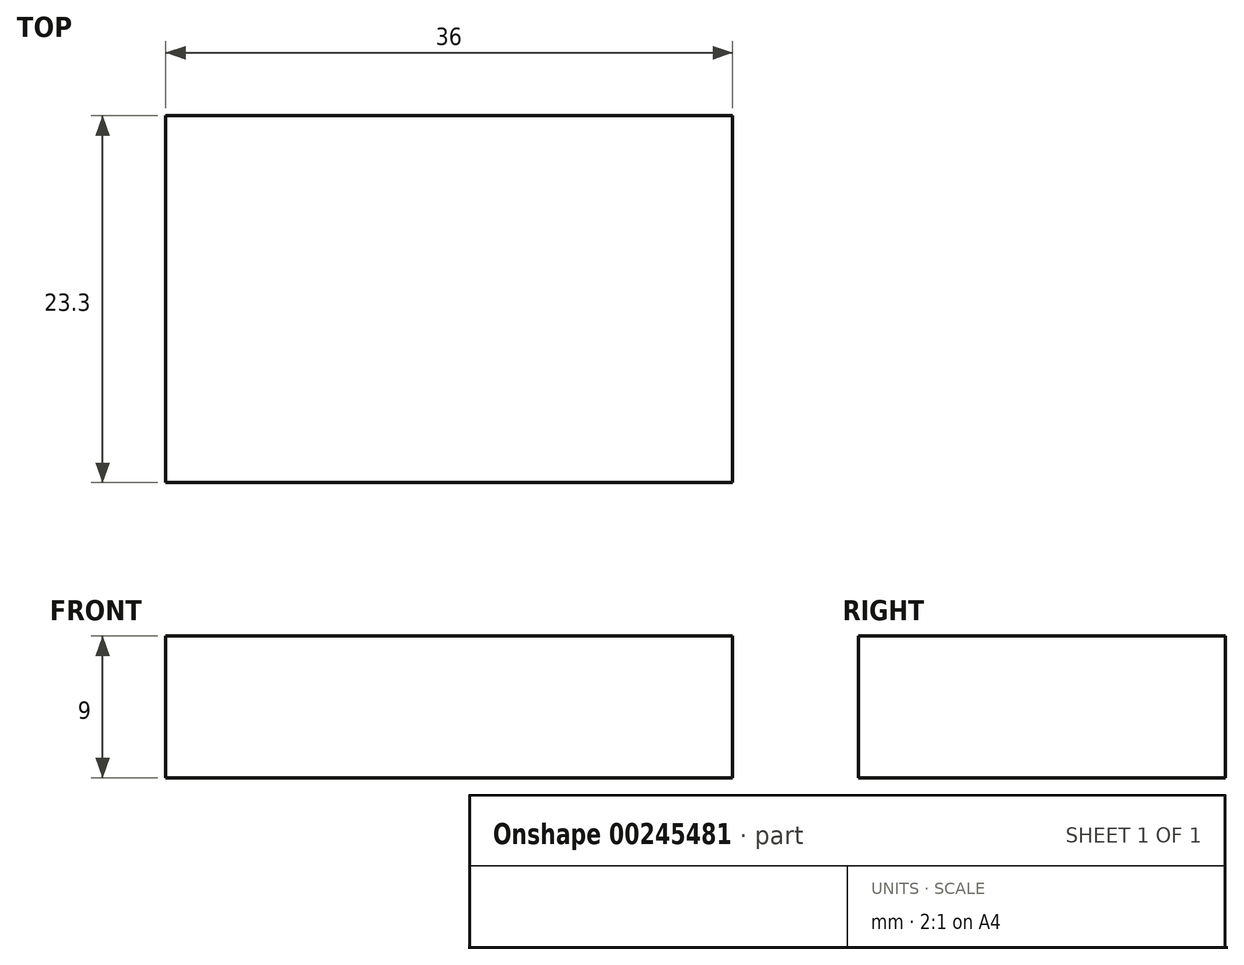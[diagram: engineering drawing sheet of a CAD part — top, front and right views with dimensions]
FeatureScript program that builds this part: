
annotation { "Feature Type Name" : "Feature", "Feature Type Description" : "" }
export const myFeature = defineFeature(function(context is Context, id is Id, definition is map)
    precondition{}
    {
        {
            var Q0;
            Q0=qCreatedBy(makeId("Top.planeOp"),FACE);
            var sketch = newSketch(context, id + "F0", { "sketchPlane" : qUnion([Q0])});
            skLineSegment(sketch, "E0.bottom", {"start": v(0, 0) * mm, "end": v(36, 0) * mm});
            skLineSegment(sketch, "E0.top", {"start": v(0, 23.3) * mm, "end": v(36, 23.3) * mm});
            skLineSegment(sketch, "E0.left", {"start": v(0, 0) * mm, "end": v(0, 23.3) * mm});
            skLineSegment(sketch, "E0.right", {"start": v(36, 0) * mm, "end": v(36, 23.3) * mm});
            skSolve(sketch);
        }
        {
            var Q0;
            Q0 = qSketchRegion(id + "F0", true);
            extrude(context, id + "F1", {"entities" : qUnion([Q0]), "depth" : 9 * mm});
        }
    });
